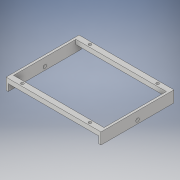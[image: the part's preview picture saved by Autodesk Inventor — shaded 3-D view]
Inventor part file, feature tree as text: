
AUTODESK INVENTOR PART (.ipt)
format: ipt  version: 2019 (Build 230136000, 136)  size: 144,896 bytes
history: native  units: in
note: dims shown in document units (in); Inventor stores cm internally (conversion verified against a paired STEP export)
features: sketch x4, extrude x2, hole x2
ambient origin geometry x8: Origin, YZ Plane, XZ Plane, XY Plane, X Axis, Y Axis, Z Axis, Center Point
bodies: Solid1 (feature_tree)
feature tree (8):
  extrude  "Extrusion1"  Depth=3.2283in
  extrude  "Extrusion2"  Depth=2.7559in
  hole  "Hole1"  [1 undecoded]
  hole  "Hole2"  [1 undecoded]
  sketch  "Sketch1"  dims[d0=4.2in d1=3.2283in]
  sketch  "Sketch2"  dims[d2=4.0in d3=2.7559in]
  sketch  "Sketch3"  dims[d4=0.2in d5=0.0in d6=0.3in d7=0.0in]
  sketch  "Sketch4"  dims[d8=3.1496in d9=3.1496in d10=0.15in d13=0.12in d14=0.625in d15=0.375in d16=0.25in d17=0.5635in d18=1.0in d19=0.8108in d20=0.15in d21=0.625in d22=0.375in d23=0.25in d24=0.5635in d25=1.0in d26=0.8108in]
note: 2 required parameter values undecoded (feature->parameter linkage not recoverable at this tier; creation-order binding heuristic only, values carry confidence <= 0.55)
